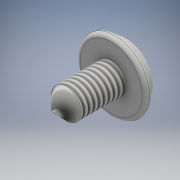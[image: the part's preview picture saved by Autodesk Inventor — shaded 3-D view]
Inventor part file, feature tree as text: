
AUTODESK INVENTOR PART (.ipt)
format: ipt  version: 2016 (Build 200138000, 138)  size: 199,168 bytes
history: native  units: mm
features: extrude x4, sketch x4, fillet x3, thread x2, chamfer x1
ambient origin geometry x8: Origin, YZ Plane, XZ Plane, XY Plane, X Axis, Y Axis, Z Axis, Center Point
bodies: Solid1 (feature_tree)
feature tree (14):
  extrude  "Extrusion1"  Depth=0.75mm TaperAngle=0.0deg
  extrude  "Extrusion2"  Depth=1.0mm TaperAngle=0.0deg
  fillet  "Fillet1"  Radius=1.0mm
  fillet  "Fillet2"  Radius=0.4mm
  extrude  "Extrusion3"  Depth=10.0mm TaperAngle=0.0deg
  chamfer  "Chamfer1"  Distance=1.5mm Angle=45.0deg
  thread  "Thread1"  [1 undecoded]
  thread  "Thread2"  [1 undecoded]
  extrude  "Extrusion4"  Depth=0.5mm
  fillet  "Fillet3"  Radius=1.0mm
  sketch  "Sketch1"  dims[d0=7.0mm d1=0.75mm d2=0.0mm]
  sketch  "Sketch2"  dims[d3=6.0mm d4=1.0mm d5=0.0mm d6=1.0mm d7=0.4mm]
  sketch  "Sketch3"  dims[d8=3.0mm d9=6.0mm d10=0.0mm d11=1.5mm d12=2.0mm d13=45.0deg d14=10.0mm d15=0.0mm d16=10.0mm d17=0.0mm]
  sketch  "Sketch4"  dims[d18=1.0mm d19=4.0mm d20=1.0mm d21=0.5mm d22=0.0mm d23=0.5mm]
note: 2 required parameter values undecoded (feature->parameter linkage not recoverable at this tier; creation-order binding heuristic only, values carry confidence <= 0.55)
